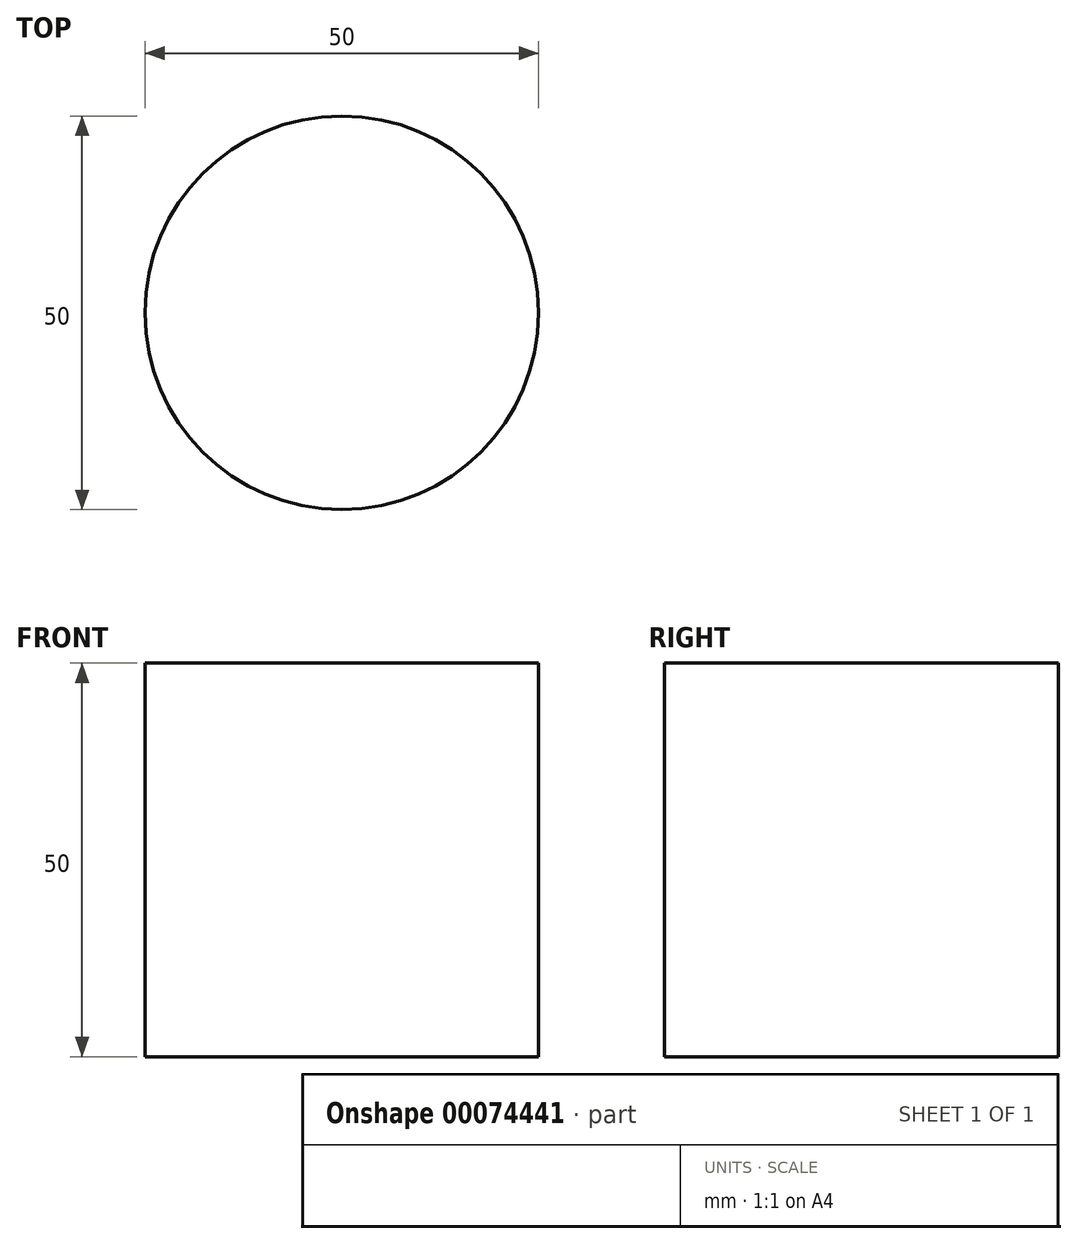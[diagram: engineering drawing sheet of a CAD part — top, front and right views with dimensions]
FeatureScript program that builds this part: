
annotation { "Feature Type Name" : "Feature", "Feature Type Description" : "" }
export const myFeature = defineFeature(function(context is Context, id is Id, definition is map)
    precondition{}
    {
        {
            var Q0;
            Q0=qCreatedBy(makeId("Top.planeOp"),FACE);
            var sketch = newSketch(context, id + "F0", { "sketchPlane" : qUnion([Q0])});
            skCircle(sketch, "E0", {"center": v(0, 0) * mm, "radius": 25 * mm});
            skLineSegment(sketch, "E1.bottom", {"start": v(63.57, 46.79) * mm, "end": v(98.57, 46.79) * mm});
            skLineSegment(sketch, "E1.top", {"start": v(63.57, 26.79) * mm, "end": v(98.57, 26.79) * mm});
            skLineSegment(sketch, "E1.left", {"start": v(63.57, 46.79) * mm, "end": v(63.57, 26.79) * mm});
            skLineSegment(sketch, "E1.right", {"start": v(98.57, 46.79) * mm, "end": v(98.57, 26.79) * mm});
            skLineSegment(sketch, "E2", {"start": v(-152.32, 56.3) * mm, "end": v(-152.32, 31.3) * mm, "construction": true});
            skLineSegment(sketch, "E3", {"start": v(-152.32, 31.3) * mm, "end": v(-102.32, 31.3) * mm, "construction": true});
            skLineSegment(sketch, "E4", {"start": v(-102.32, 31.3) * mm, "end": v(-102.32, 56.3) * mm, "construction": true});
            skPoint(sketch, "E5.end.orphan", {"position": v(-25, 0) * mm});
            skLineSegment(sketch, "E6", {"start": v(-102.32, 56.3) * mm, "end": v(-152.32, 56.3) * mm, "construction": true});
            skLineSegment(sketch, "E7", {"start": v(0, 84.9) * mm, "end": v(0, -89.8) * mm, "construction": true});
            skSolve(sketch);
        }
        {
            var Q0;
            Q0=makeQuery(id+"F0.imprint","IMPRINT",FACE,{"disambiguationData":[TD([[makeQuery(id+"F0.imprint","IMPRINT",EDGE,{"derivedFrom":sQuery(id+"F0.wireOp",EDGE,"E0")}),1.0]])]});
            extrude(context, id + "F1", {"entities" : qUnion([Q0]), "depth" : 50 * mm});
        }
    });
